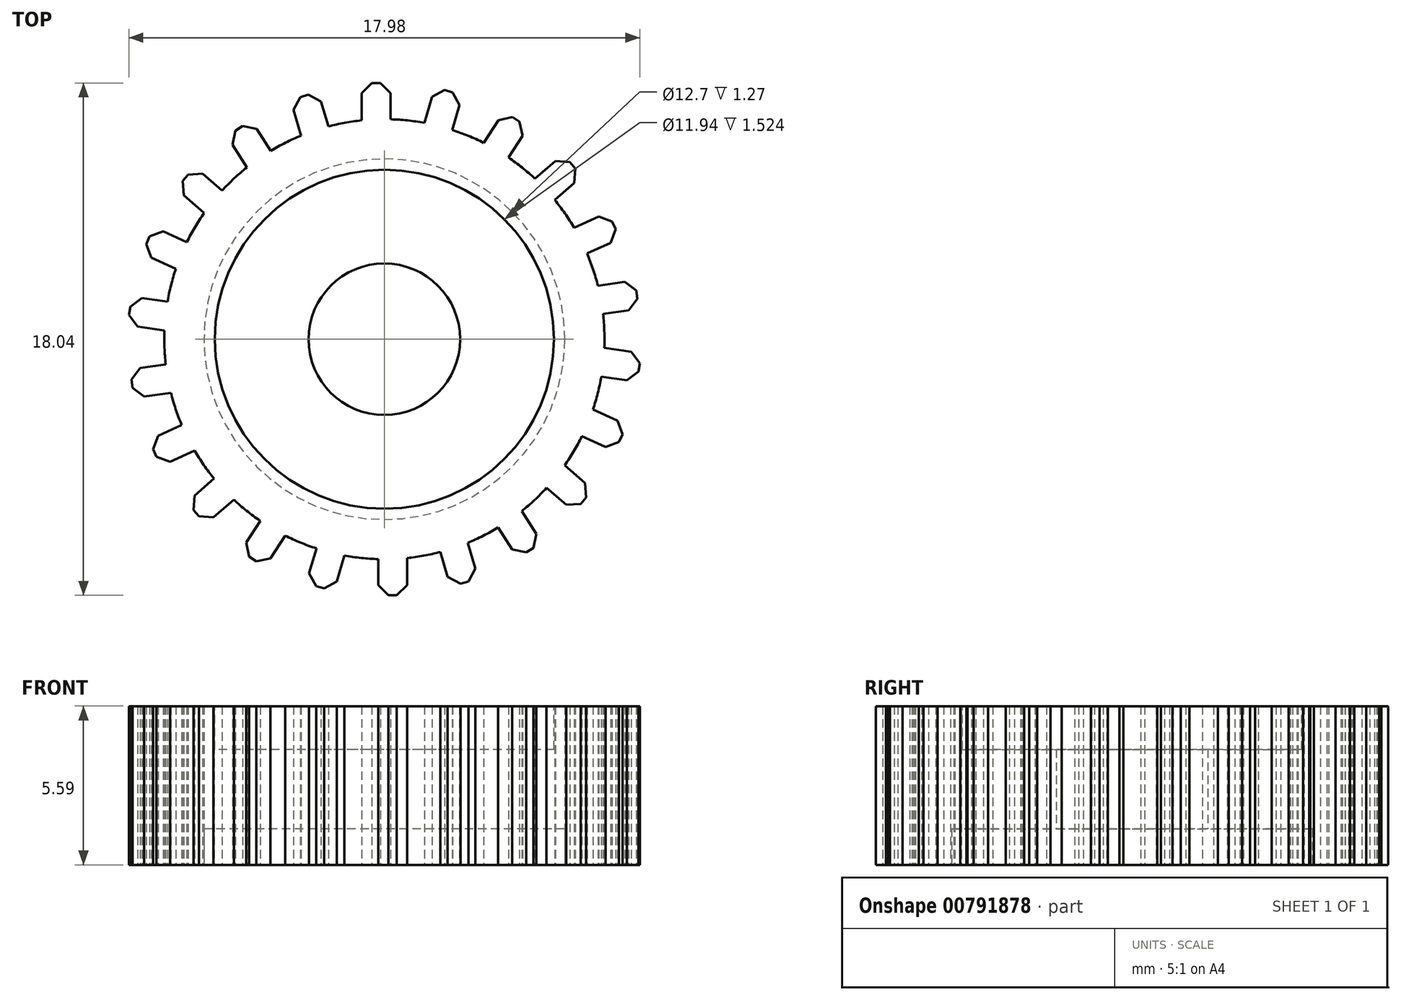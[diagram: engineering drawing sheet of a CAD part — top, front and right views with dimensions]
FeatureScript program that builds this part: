
annotation { "Feature Type Name" : "Feature", "Feature Type Description" : "" }
export const myFeature = defineFeature(function(context is Context, id is Id, definition is map)
    precondition{}
    {
        {
            var Q0;
            Q0=qCreatedBy(makeId("Top.planeOp"),FACE);
            var sketch = newSketch(context, id + "F0", { "sketchPlane" : qUnion([Q0])});
            skCircle(sketch, "E0", {"center": v(0, 0) * mm, "radius": 7.75 * mm});
            skLineSegment(sketch, "E1", {"start": v(-0.8, 7.7) * mm, "end": v(-0.8, 8.66) * mm});
            skLineSegment(sketch, "E2", {"start": v(-0.8, 8.66) * mm, "end": v(-0.44, 9.02) * mm});
            skLineSegment(sketch, "E3", {"start": v(-0.14, 9.02) * mm, "end": v(0, 8.88) * mm});
            skLineSegment(sketch, "E4", {"start": v(0.22, 8.66) * mm, "end": v(0.22, 7.74) * mm});
            skLineSegment(sketch, "E5", {"start": v(-0.44, 9.02) * mm, "end": v(-0.14, 9.02) * mm});
            skLineSegment(sketch, "E6.trimOffspring", {"start": v(-0.72, 8.74) * mm, "end": v(-0.44, 9.02) * mm});
            skLineSegment(sketch, "E7.trimOffspring", {"start": v(-0.14, 9.02) * mm, "end": v(0.22, 8.66) * mm});
            skCircle(sketch, "E8", {"center": v(0, 0) * mm, "radius": 2.67 * mm});
            skSolve(sketch);
        }
        {
            var Q0;
            {var subQ0=sQuery(id+"F0.wireOp",EDGE,"E0");var subQ1=makeQuery(id+"F0.imprint","INTERSECT",VERTEX,{"derivedFrom":[subQ0,sQuery(id+"F0.wireOp",EDGE,"E1")]});Q0=makeQuery(id+"F0.imprint","IMPRINT",FACE,{"disambiguationData":[TD([[makeQuery(id+"F0.imprint","IMPRINT",EDGE,{"disambiguationData":[TD([[subQ1,1.0]])],"derivedFrom":subQ0}),1.0]])]});}
            extrude(context, id + "F1", {"entities" : qUnion([Q0]), "depth" : 5.6 * mm, "offsetDistance" : 25.4 * mm});
        }
        {
            var Q0;
            {var subQ1=sQuery(id+"F0.wireOp",EDGE,"E1");Q0=makeQuery(id+"F0.imprint","IMPRINT",FACE,{"disambiguationData":[TD([[makeQuery(id+"F0.imprint","IMPRINT",EDGE,{"derivedFrom":subQ1}),-1.0]])]});}
            extrude(context, id + "F2", {"entities" : qUnion([Q0]), "depth" : 5.6 * mm, "offsetDistance" : 25.4 * mm});
        }
        {
            var Q0;
            Q0=makeQuery(id+"F2.opExtrude","SWEPT_BODY",BODY,{"disambiguationData":[OSD([sQuery(id+"F0.wireOp",EDGE,"E0"),sQuery(id+"F0.wireOp",EDGE,"E1"),sQuery(id+"F0.wireOp",EDGE,"E2"),sQuery(id+"F0.wireOp",EDGE,"E3"),sQuery(id+"F0.wireOp",EDGE,"E4"),sQuery(id+"F0.wireOp",EDGE,"E5"),sQuery(id+"F0.wireOp",EDGE,"E7.trimOffspring")])]});
            var Q1;
            Q1=makeQuery(id+"F1.opExtrude","SWEPT_FACE",FACE,{"disambiguationData":[OSD([sQuery(id+"F0.wireOp",EDGE,"E0")])]});
            circularPattern(context, id + "F3", {"operationType" : NewBodyOperationType.ADD, "entities" : qUnion([Q0]), "axis" : qUnion([Q1]), "angle" : 360 * degree, "instanceCount" : 22, "equalSpace" : true, "isCentered" : true, "fullFeaturePattern" : false, "computeTransformsWithoutBuiltin" : true});
        }
        {
            var Q0;
            {var subQ0=sQuery(id+"F0.wireOp",EDGE,"E0");var subQ1=makeQuery(id+"F2.opExtrude","CAP_FACE",FACE,{"disambiguationData":[OSD([subQ0,sQuery(id+"F0.wireOp",EDGE,"E1"),sQuery(id+"F0.wireOp",EDGE,"E2"),sQuery(id+"F0.wireOp",EDGE,"E3"),sQuery(id+"F0.wireOp",EDGE,"E4"),sQuery(id+"F0.wireOp",EDGE,"E5"),sQuery(id+"F0.wireOp",EDGE,"E7.trimOffspring")])],"isStart":false});Q0=makeQuery(id+"F3.boolean.opBoolean","MERGE",FACE,{"derivedFrom":[makeQuery(id+"F1.opExtrude","CAP_FACE",FACE,{"disambiguationData":[OSD([subQ0,sQuery(id+"F0.wireOp",EDGE,"E8")])],"isStart":false}),subQ1,makeQuery(id+"F3.opPattern","COPY",FACE,{"derivedFrom":subQ1,"instanceName":"-21"}),makeQuery(id+"F3.opPattern","COPY",FACE,{"derivedFrom":subQ1,"instanceName":"-20"}),makeQuery(id+"F3.opPattern","COPY",FACE,{"derivedFrom":subQ1,"instanceName":"-19"}),makeQuery(id+"F3.opPattern","COPY",FACE,{"derivedFrom":subQ1,"instanceName":"-18"}),makeQuery(id+"F3.opPattern","COPY",FACE,{"derivedFrom":subQ1,"instanceName":"-17"}),makeQuery(id+"F3.opPattern","COPY",FACE,{"derivedFrom":subQ1,"instanceName":"-16"}),makeQuery(id+"F3.opPattern","COPY",FACE,{"derivedFrom":subQ1,"instanceName":"-15"}),makeQuery(id+"F3.opPattern","COPY",FACE,{"derivedFrom":subQ1,"instanceName":"-14"}),makeQuery(id+"F3.opPattern","COPY",FACE,{"derivedFrom":subQ1,"instanceName":"-13"}),makeQuery(id+"F3.opPattern","COPY",FACE,{"derivedFrom":subQ1,"instanceName":"-12"}),makeQuery(id+"F3.opPattern","COPY",FACE,{"derivedFrom":subQ1,"instanceName":"-11"}),makeQuery(id+"F3.opPattern","COPY",FACE,{"derivedFrom":subQ1,"instanceName":"-10"}),makeQuery(id+"F3.opPattern","COPY",FACE,{"derivedFrom":subQ1,"instanceName":"-9"}),makeQuery(id+"F3.opPattern","COPY",FACE,{"derivedFrom":subQ1,"instanceName":"-8"}),makeQuery(id+"F3.opPattern","COPY",FACE,{"derivedFrom":subQ1,"instanceName":"-7"}),makeQuery(id+"F3.opPattern","COPY",FACE,{"derivedFrom":subQ1,"instanceName":"-6"}),makeQuery(id+"F3.opPattern","COPY",FACE,{"derivedFrom":subQ1,"instanceName":"-5"}),makeQuery(id+"F3.opPattern","COPY",FACE,{"derivedFrom":subQ1,"instanceName":"-4"}),makeQuery(id+"F3.opPattern","COPY",FACE,{"derivedFrom":subQ1,"instanceName":"-3"}),makeQuery(id+"F3.opPattern","COPY",FACE,{"derivedFrom":subQ1,"instanceName":"-2"}),makeQuery(id+"F3.opPattern","COPY",FACE,{"derivedFrom":subQ1,"instanceName":"-1"})]});}
            var sketch = newSketch(context, id + "F4", { "sketchPlane" : qUnion([Q0])});
            skCircle(sketch, "E9", {"center": v(0, 0) * mm, "radius": 5.97 * mm});
            skSolve(sketch);
        }
        {
            var Q0;
            Q0=makeQuery(id+"F0.imprint","IMPRINT",FACE,{"disambiguationData":[TD([[makeQuery(id+"F0.imprint","IMPRINT",EDGE,{"derivedFrom":sQuery(id+"F0.wireOp",EDGE,"E8")}),-1.0]])]});
            var sketch = newSketch(context, id + "F5", { "sketchPlane" : qUnion([Q0])});
            skCircle(sketch, "E10", {"center": v(0, 0) * mm, "radius": 6.35 * mm});
            skSolve(sketch);
        }
        {
            var Q0;
            Q0=makeQuery(id+"F5.imprint","IMPRINT",FACE,{"disambiguationData":[TD([[makeQuery(id+"F5.imprint","IMPRINT",EDGE,{"derivedFrom":sQuery(id+"F5.wireOp",EDGE,"E10")}),1.0]])]});
            extrude(context, id + "F6", {"entities" : qUnion([Q0]), "operationType" : NewBodyOperationType.REMOVE, "depth" : 1.27 * mm, "offsetDistance" : 25.4 * mm});
        }
        {
            var Q0;
            Q0=makeQuery(id+"F4.imprint","IMPRINT",FACE,{"disambiguationData":[TD([[makeQuery(id+"F4.imprint","IMPRINT",EDGE,{"derivedFrom":sQuery(id+"F4.wireOp",EDGE,"E9")}),1.0]])]});
            extrude(context, id + "F7", {"entities" : qUnion([Q0]), "operationType" : NewBodyOperationType.REMOVE, "oppositeDirection" : true, "depth" : 1.52 * mm, "offsetDistance" : 25.4 * mm});
        }
    });
